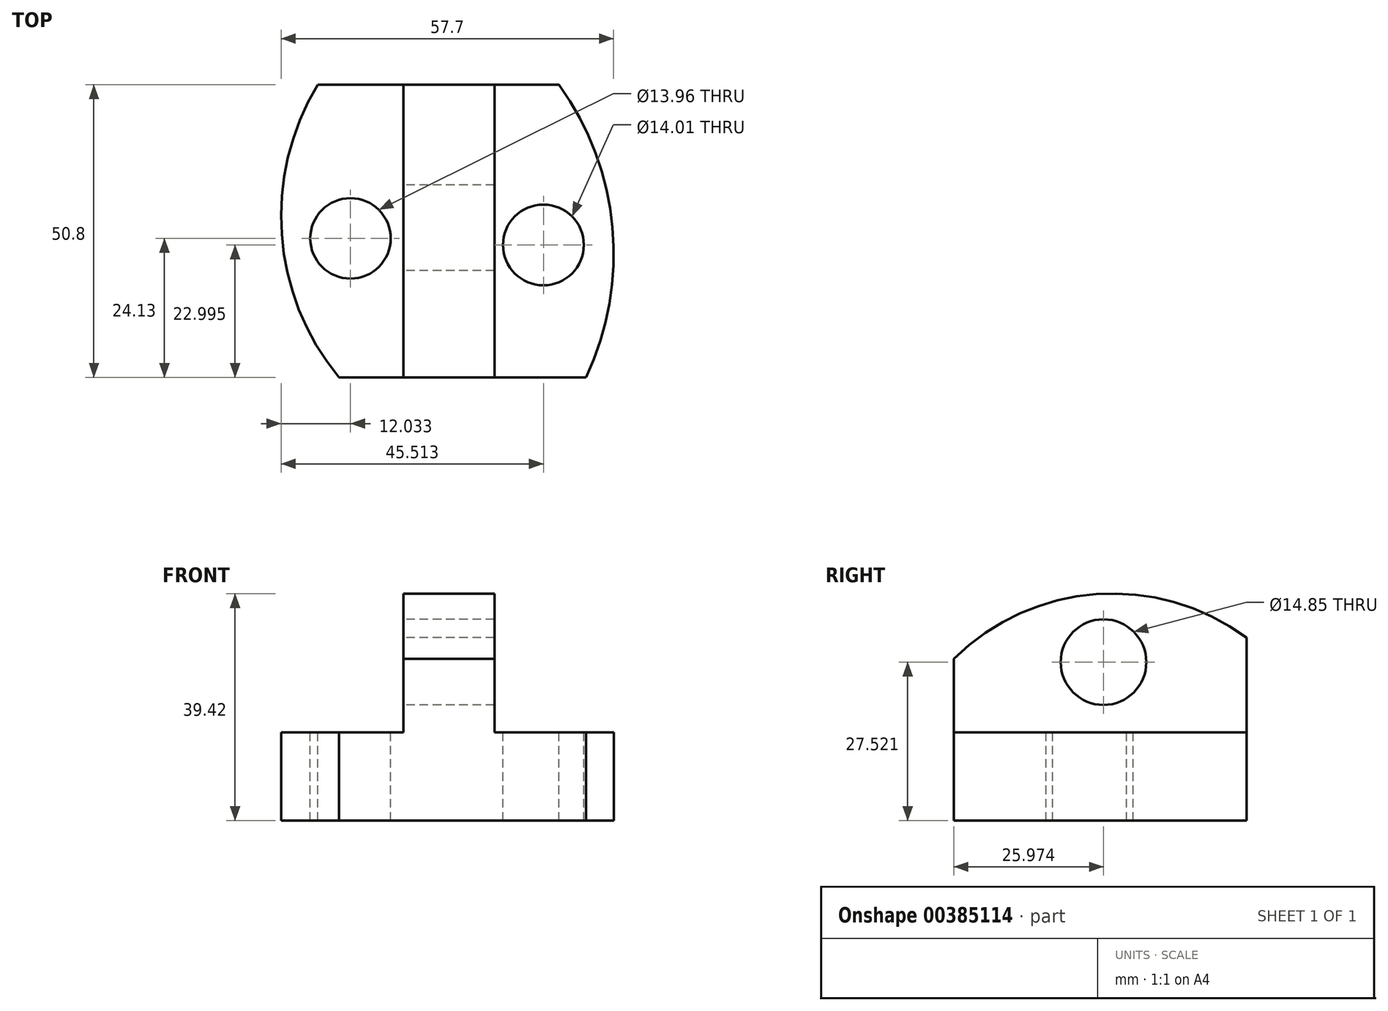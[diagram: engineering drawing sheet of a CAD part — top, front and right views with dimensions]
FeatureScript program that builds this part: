
annotation { "Feature Type Name" : "Feature", "Feature Type Description" : "" }
export const myFeature = defineFeature(function(context is Context, id is Id, definition is map)
    precondition{}
    {
        {
            var Q0;
            Q0=qCreatedBy(makeId("Front.planeOp"),FACE);
            var sketch = newSketch(context, id + "F0", { "sketchPlane" : qUnion([Q0])});
            skLineSegment(sketch, "E0", {"start": v(0, 0) * mm, "end": v(0, 40.86) * mm});
            skLineSegment(sketch, "E1", {"start": v(0, 40.86) * mm, "end": v(60.57, 40.86) * mm});
            skLineSegment(sketch, "E2", {"start": v(60.57, 40.86) * mm, "end": v(60.57, 0) * mm});
            skLineSegment(sketch, "E3", {"start": v(60.57, 0) * mm, "end": v(0, 0) * mm});
            skSolve(sketch);
        }
        {
            var Q0;
            Q0 = qSketchRegion(id + "F0", true);
            extrude(context, id + "F1", {"entities" : qUnion([Q0]), "depth" : 50.8 * mm});
        }
        {
            var Q0;
            Q0=makeQuery(id+"F1.opExtrude","CAP_FACE",FACE,{"disambiguationData":[OSD([sQuery(id+"F0.wireOp",EDGE,"E0"),sQuery(id+"F0.wireOp",EDGE,"E1"),sQuery(id+"F0.wireOp",EDGE,"E2"),sQuery(id+"F0.wireOp",EDGE,"E3")])],"isStart":false});
            var sketch = newSketch(context, id + "F2", { "sketchPlane" : qUnion([Q0])});
            skLineSegment(sketch, "E4", {"start": v(38.16, 40.86) * mm, "end": v(38.16, 15.33) * mm});
            skLineSegment(sketch, "E5", {"start": v(38.16, 15.33) * mm, "end": v(60.57, 15.33) * mm});
            skLineSegment(sketch, "E6", {"start": v(22.4, 40.86) * mm, "end": v(22.4, 15.32) * mm});
            skLineSegment(sketch, "E7", {"start": v(22.4, 15.32) * mm, "end": v(0, 15.32) * mm});
            skSolve(sketch);
        }
        {
            var Q0;
            {var subQ0=sQuery(id+"F2.wireOp",EDGE,"E6");Q0=makeQuery(id+"F2.imprint","IMPRINT",FACE,{"disambiguationData":[TD([[makeQuery(id+"F2.imprint","IMPRINT",EDGE,{"derivedFrom":subQ0}),-1.0]])]});}
            var Q1;
            {var subQ0=sQuery(id+"F2.wireOp",EDGE,"E4");Q1=makeQuery(id+"F2.imprint","IMPRINT",FACE,{"disambiguationData":[TD([[makeQuery(id+"F2.imprint","IMPRINT",EDGE,{"derivedFrom":subQ0}),1.0]])]});}
            extrude(context, id + "F3", {"entities" : qUnion([Q0, Q1]), "operationType" : NewBodyOperationType.REMOVE, "oppositeDirection" : true, "depth" : 50.8 * mm});
        }
        {
            var Q0;
            Q0=makeQuery(id+"F3.boolean.opBoolean","COPY",FACE,{"derivedFrom":makeQuery(id+"F3.opExtrude","SWEPT_FACE",FACE,{"disambiguationData":[OSD([sQuery(id+"F2.wireOp",EDGE,"E6")])]})});
            var sketch = newSketch(context, id + "F4", { "sketchPlane" : qUnion([Q0])});
            skArc(sketch, "E8", {"start": v(50.8, 28.09) * mm, "mid": v(26.08, 39.32) * mm, "end": v(0, 31.78) * mm});
            skSolve(sketch);
        }
        {
            var Q0;
            {var subQ0=sQuery(id+"F4.wireOp",EDGE,"E8");Q0=makeQuery(id+"F4.imprint","IMPRINT",FACE,{"disambiguationData":[TD([[makeQuery(id+"F4.imprint","IMPRINT",EDGE,{"derivedFrom":subQ0}),-1.0]])]});}
            extrude(context, id + "F5", {"entities" : qUnion([Q0]), "operationType" : NewBodyOperationType.REMOVE, "oppositeDirection" : true, "depth" : 25.4 * mm});
        }
        {
            var Q0;
            Q0=makeQuery(id+"F3.boolean.opBoolean","COPY",FACE,{"derivedFrom":makeQuery(id+"F3.opExtrude","SWEPT_FACE",FACE,{"disambiguationData":[OSD([sQuery(id+"F2.wireOp",EDGE,"E7")])]})});
            var sketch = newSketch(context, id + "F6", { "sketchPlane" : qUnion([Q0])});
            skArc(sketch, "E9", {"start": v(7.52, 0) * mm, "mid": v(1.27, -25.99) * mm, "end": v(11.2, -50.8) * mm});
            skSolve(sketch);
        }
        {
            var Q0;
            {var subQ0=sQuery(id+"F6.wireOp",EDGE,"E9");Q0=makeQuery(id+"F6.imprint","IMPRINT",FACE,{"disambiguationData":[TD([[makeQuery(id+"F6.imprint","IMPRINT",EDGE,{"derivedFrom":subQ0}),-1.0]])]});}
            extrude(context, id + "F7", {"entities" : qUnion([Q0]), "operationType" : NewBodyOperationType.REMOVE, "oppositeDirection" : true, "depth" : 25.4 * mm});
        }
        {
            var Q0;
            Q0=makeQuery(id+"F3.boolean.opBoolean","COPY",FACE,{"derivedFrom":makeQuery(id+"F3.opExtrude","SWEPT_FACE",FACE,{"disambiguationData":[OSD([sQuery(id+"F2.wireOp",EDGE,"E5")])]})});
            var sketch = newSketch(context, id + "F8", { "sketchPlane" : qUnion([Q0])});
            skArc(sketch, "E10", {"start": v(54.05, -50.8) * mm, "mid": v(58.65, -24.76) * mm, "end": v(49.37, 0) * mm});
            skSolve(sketch);
        }
        {
            var Q0;
            {var subQ0=sQuery(id+"F8.wireOp",EDGE,"E10");Q0=makeQuery(id+"F8.imprint","IMPRINT",FACE,{"disambiguationData":[TD([[makeQuery(id+"F8.imprint","IMPRINT",EDGE,{"derivedFrom":subQ0}),-1.0]])]});}
            extrude(context, id + "F9", {"entities" : qUnion([Q0]), "operationType" : NewBodyOperationType.REMOVE, "oppositeDirection" : true, "depth" : 25.4 * mm});
        }
        {
            var Q0;
            Q0=makeQuery(id+"F3.boolean.opBoolean","COPY",FACE,{"derivedFrom":makeQuery(id+"F3.opExtrude","SWEPT_FACE",FACE,{"disambiguationData":[OSD([sQuery(id+"F2.wireOp",EDGE,"E6")])]})});
            var sketch = newSketch(context, id + "F10", { "sketchPlane" : qUnion([Q0])});
            skCircle(sketch, "E11", {"center": v(24.83, 27.52) * mm, "radius": 7.43 * mm});
            skSolve(sketch);
        }
        {
            var Q0;
            Q0=makeQuery(id+"F10.imprint","IMPRINT",FACE,{"disambiguationData":[TD([[makeQuery(id+"F10.imprint","IMPRINT",EDGE,{"derivedFrom":sQuery(id+"F10.wireOp",EDGE,"E11")}),1.0]])]});
            extrude(context, id + "F11", {"entities" : qUnion([Q0]), "operationType" : NewBodyOperationType.REMOVE, "oppositeDirection" : true, "depth" : 25.4 * mm});
        }
        {
            var Q0;
            Q0=makeQuery(id+"F3.boolean.opBoolean","COPY",FACE,{"derivedFrom":makeQuery(id+"F3.opExtrude","SWEPT_FACE",FACE,{"disambiguationData":[OSD([sQuery(id+"F2.wireOp",EDGE,"E7")])]})});
            var sketch = newSketch(context, id + "F12", { "sketchPlane" : qUnion([Q0])});
            skCircle(sketch, "E12", {"center": v(13.2, -26.67) * mm, "radius": 6.98 * mm});
            skCircle(sketch, "E13", {"center": v(47.52, -27.52) * mm, "radius": 7.14 * mm});
            skSolve(sketch);
        }
        {
            var Q0;
            Q0=makeQuery(id+"F12.imprint","IMPRINT",FACE,{"disambiguationData":[TD([[makeQuery(id+"F12.imprint","IMPRINT",EDGE,{"derivedFrom":sQuery(id+"F12.wireOp",EDGE,"E12")}),1.0]])]});
            extrude(context, id + "F13", {"entities" : qUnion([Q0]), "operationType" : NewBodyOperationType.REMOVE, "oppositeDirection" : true, "depth" : 25.4 * mm});
        }
        {
            var Q0;
            Q0=makeQuery(id+"F3.boolean.opBoolean","COPY",FACE,{"derivedFrom":makeQuery(id+"F3.opExtrude","SWEPT_FACE",FACE,{"disambiguationData":[OSD([sQuery(id+"F2.wireOp",EDGE,"E5")])]})});
            var sketch = newSketch(context, id + "F14", { "sketchPlane" : qUnion([Q0])});
            skCircle(sketch, "E14", {"center": v(46.67, -27.8) * mm, "radius": 7 * mm});
            skSolve(sketch);
        }
        {
            var Q0;
            Q0=makeQuery(id+"F14.imprint","IMPRINT",FACE,{"disambiguationData":[TD([[makeQuery(id+"F14.imprint","IMPRINT",EDGE,{"derivedFrom":sQuery(id+"F14.wireOp",EDGE,"E14")}),1.0]])]});
            extrude(context, id + "F15", {"entities" : qUnion([Q0]), "operationType" : NewBodyOperationType.REMOVE, "oppositeDirection" : true, "depth" : 25.4 * mm});
        }
    });
